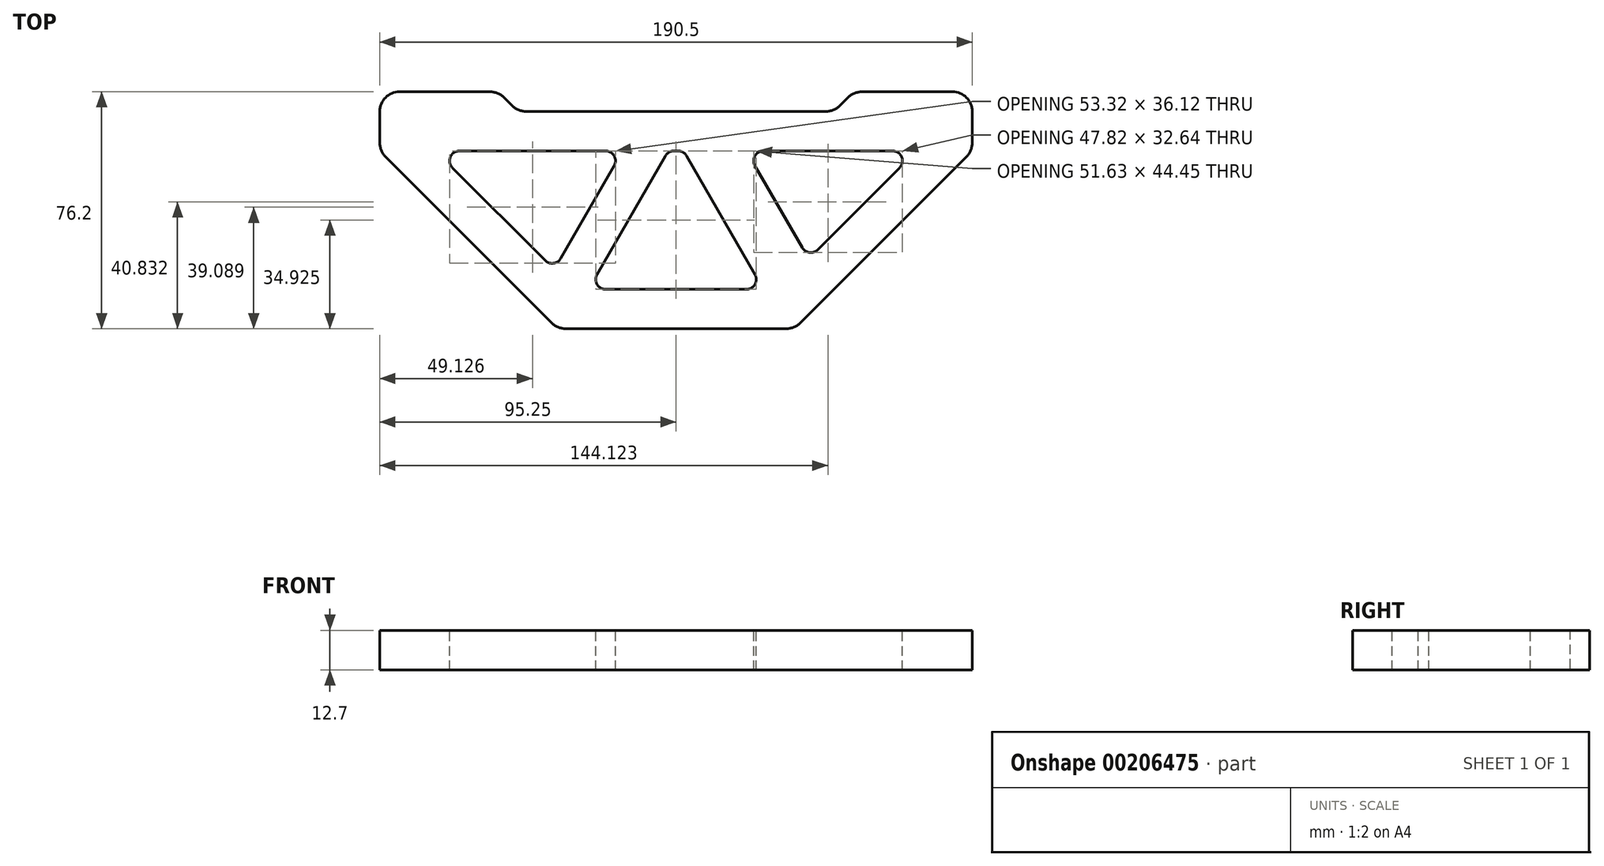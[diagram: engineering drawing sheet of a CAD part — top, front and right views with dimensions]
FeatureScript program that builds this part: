
annotation { "Feature Type Name" : "Feature", "Feature Type Description" : "" }
export const myFeature = defineFeature(function(context is Context, id is Id, definition is map)
    precondition{}
    {
        {
            var Q0;
            Q0=qCreatedBy(makeId("Top.planeOp"),FACE);
            var sketch = newSketch(context, id + "F0", { "sketchPlane" : qUnion([Q0])});
            skLineSegment(sketch, "E0", {"start": v(-82.55, 31.75) * mm, "end": v(-53.43, 31.75) * mm});
            skLineSegment(sketch, "E1", {"start": v(-48.94, 29.9) * mm, "end": v(-46.3, 27.26) * mm});
            skLineSegment(sketch, "E2", {"start": v(-41.82, 25.4) * mm, "end": v(54.52, 25.4) * mm});
            skLineSegment(sketch, "E3", {"start": v(59, 27.26) * mm, "end": v(61.64, 29.9) * mm});
            skLineSegment(sketch, "E4", {"start": v(66.13, 31.75) * mm, "end": v(95.25, 31.75) * mm});
            skLineSegment(sketch, "E5", {"start": v(101.6, 25.4) * mm, "end": v(101.6, 15.33) * mm});
            skLineSegment(sketch, "E6", {"start": v(99.74, 10.84) * mm, "end": v(46.3, -42.6) * mm});
            skLineSegment(sketch, "E7", {"start": v(41.82, -44.45) * mm, "end": v(-29.12, -44.45) * mm});
            skLineSegment(sketch, "E8", {"start": v(-33.6, -42.6) * mm, "end": v(-87.04, 10.84) * mm});
            skLineSegment(sketch, "E9", {"start": v(-88.9, 15.33) * mm, "end": v(-88.9, 25.4) * mm});
            skPoint(sketch, "E10.visualSharp", {"position": v(-88.9, 31.75) * mm});
            skArc(sketch, "E10.filletArc", {"start": v(-82.55, 31.75) * mm, "mid": v(-87.04, 29.9) * mm, "end": v(-88.9, 25.4) * mm});
            skPoint(sketch, "E11.visualSharp", {"position": v(-88.9, 12.7) * mm});
            skArc(sketch, "E11.filletArc", {"start": v(-88.9, 15.33) * mm, "mid": v(-88.42, 12.9) * mm, "end": v(-87.04, 10.84) * mm});
            skPoint(sketch, "E12.visualSharp", {"position": v(-31.75, -44.45) * mm});
            skArc(sketch, "E12.filletArc", {"start": v(-33.6, -42.6) * mm, "mid": v(-31.55, -43.97) * mm, "end": v(-29.12, -44.45) * mm});
            skPoint(sketch, "E13.visualSharp", {"position": v(44.45, -44.45) * mm});
            skArc(sketch, "E13.filletArc", {"start": v(41.82, -44.45) * mm, "mid": v(44.25, -43.97) * mm, "end": v(46.3, -42.6) * mm});
            skPoint(sketch, "E14.visualSharp", {"position": v(101.6, 12.7) * mm});
            skArc(sketch, "E14.filletArc", {"start": v(99.74, 10.84) * mm, "mid": v(101.12, 12.9) * mm, "end": v(101.6, 15.33) * mm});
            skPoint(sketch, "E15.visualSharp", {"position": v(101.6, 31.75) * mm});
            skArc(sketch, "E15.filletArc", {"start": v(101.6, 25.4) * mm, "mid": v(99.74, 29.9) * mm, "end": v(95.25, 31.75) * mm});
            skPoint(sketch, "E16.visualSharp", {"position": v(63.5, 31.75) * mm});
            skArc(sketch, "E16.filletArc", {"start": v(66.13, 31.75) * mm, "mid": v(63.7, 31.27) * mm, "end": v(61.64, 29.9) * mm});
            skPoint(sketch, "E17.visualSharp", {"position": v(57.15, 25.4) * mm});
            skArc(sketch, "E17.filletArc", {"start": v(54.52, 25.4) * mm, "mid": v(56.95, 25.88) * mm, "end": v(59, 27.26) * mm});
            skPoint(sketch, "E18.visualSharp", {"position": v(-44.45, 25.4) * mm});
            skArc(sketch, "E18.filletArc", {"start": v(-46.3, 27.26) * mm, "mid": v(-44.25, 25.88) * mm, "end": v(-41.82, 25.4) * mm});
            skPoint(sketch, "E19.visualSharp", {"position": v(-50.8, 31.75) * mm});
            skArc(sketch, "E19.filletArc", {"start": v(-48.94, 29.9) * mm, "mid": v(-51, 31.27) * mm, "end": v(-53.43, 31.75) * mm});
            skSolve(sketch);
        }
        {
            var Q0;
            Q0 = qSketchRegion(id + "F0", true);
            extrude(context, id + "F1", {"entities" : qUnion([Q0]), "depth" : 12.7 * mm});
        }
        {
            var Q0;
            Q0=makeQuery(id+"F1.opExtrude","CAP_FACE",FACE,{"disambiguationData":[OSD([sQuery(id+"F0.wireOp",EDGE,"E0"),sQuery(id+"F0.wireOp",EDGE,"E1"),sQuery(id+"F0.wireOp",EDGE,"E2"),sQuery(id+"F0.wireOp",EDGE,"E3"),sQuery(id+"F0.wireOp",EDGE,"E4"),sQuery(id+"F0.wireOp",EDGE,"E5"),sQuery(id+"F0.wireOp",EDGE,"E6"),sQuery(id+"F0.wireOp",EDGE,"E7"),sQuery(id+"F0.wireOp",EDGE,"E8"),sQuery(id+"F0.wireOp",EDGE,"E9"),sQuery(id+"F0.wireOp",EDGE,"E10.filletArc"),sQuery(id+"F0.wireOp",EDGE,"E11.filletArc"),sQuery(id+"F0.wireOp",EDGE,"E12.filletArc"),sQuery(id+"F0.wireOp",EDGE,"E13.filletArc"),sQuery(id+"F0.wireOp",EDGE,"E14.filletArc"),sQuery(id+"F0.wireOp",EDGE,"E15.filletArc"),sQuery(id+"F0.wireOp",EDGE,"E16.filletArc"),sQuery(id+"F0.wireOp",EDGE,"E17.filletArc"),sQuery(id+"F0.wireOp",EDGE,"E18.filletArc"),sQuery(id+"F0.wireOp",EDGE,"E19.filletArc")])],"isStart":false});
            var sketch = newSketch(context, id + "F2", { "sketchPlane" : qUnion([Q0])});
            skLineSegment(sketch, "E20", {"start": v(2.96, 11.11) * mm, "end": v(-19.04, -26.99) * mm});
            skLineSegment(sketch, "E21", {"start": v(-16.29, -31.75) * mm, "end": v(28.99, -31.75) * mm});
            skLineSegment(sketch, "E22", {"start": v(31.74, -26.99) * mm, "end": v(9.74, 11.11) * mm});
            skLineSegment(sketch, "E23", {"start": v(5.7, 12.7) * mm, "end": v(7, 12.7) * mm});
            skLineSegment(sketch, "E24", {"start": v(31.74, 7.94) * mm, "end": v(46.92, -18.36) * mm});
            skLineSegment(sketch, "E25", {"start": v(51.92, -19.02) * mm, "end": v(78.22, 7.28) * mm});
            skLineSegment(sketch, "E26", {"start": v(75.97, 12.7) * mm, "end": v(34.49, 12.7) * mm});
            skLineSegment(sketch, "E27", {"start": v(-65.52, 7.28) * mm, "end": v(-35.73, -22.5) * mm});
            skLineSegment(sketch, "E28", {"start": v(-30.74, -21.85) * mm, "end": v(-13.54, 7.94) * mm});
            skLineSegment(sketch, "E29", {"start": v(-16.29, 12.7) * mm, "end": v(-63.27, 12.7) * mm});
            skPoint(sketch, "E30.visualSharp", {"position": v(-70.94, 12.7) * mm});
            skArc(sketch, "E30.filletArc", {"start": v(-63.27, 12.7) * mm, "mid": v(-66.2, 10.74) * mm, "end": v(-65.52, 7.28) * mm});
            skPoint(sketch, "E31.visualSharp", {"position": v(-10.79, 12.7) * mm});
            skArc(sketch, "E31.filletArc", {"start": v(-13.54, 7.94) * mm, "mid": v(-13.54, 11.11) * mm, "end": v(-16.29, 12.7) * mm});
            skPoint(sketch, "E32.visualSharp", {"position": v(-21.79, -31.75) * mm});
            skArc(sketch, "E32.filletArc", {"start": v(-19.04, -26.99) * mm, "mid": v(-19.04, -30.16) * mm, "end": v(-16.29, -31.75) * mm});
            skPoint(sketch, "E33.visualSharp", {"position": v(34.49, -31.75) * mm});
            skArc(sketch, "E33.filletArc", {"start": v(28.99, -31.75) * mm, "mid": v(31.74, -30.16) * mm, "end": v(31.74, -26.99) * mm});
            skPoint(sketch, "E34.visualSharp", {"position": v(28.99, 12.7) * mm});
            skArc(sketch, "E34.filletArc", {"start": v(34.49, 12.7) * mm, "mid": v(31.74, 11.11) * mm, "end": v(31.74, 7.94) * mm});
            skPoint(sketch, "E35.visualSharp", {"position": v(49, -21.95) * mm});
            skArc(sketch, "E35.filletArc", {"start": v(46.92, -18.36) * mm, "mid": v(49.26, -19.92) * mm, "end": v(51.92, -19.02) * mm});
            skPoint(sketch, "E36.visualSharp", {"position": v(83.64, 12.7) * mm});
            skArc(sketch, "E36.filletArc", {"start": v(78.22, 7.28) * mm, "mid": v(78.9, 10.74) * mm, "end": v(75.97, 12.7) * mm});
            skPoint(sketch, "E37.visualSharp", {"position": v(8.82, 12.7) * mm});
            skArc(sketch, "E37.filletArc", {"start": v(9.74, 11.11) * mm, "mid": v(8.58, 12.27) * mm, "end": v(7, 12.7) * mm});
            skPoint(sketch, "E38.visualSharp", {"position": v(-32.8, -25.43) * mm});
            skArc(sketch, "E38.filletArc", {"start": v(-35.73, -22.5) * mm, "mid": v(-33.07, -23.41) * mm, "end": v(-30.74, -21.85) * mm});
            skPoint(sketch, "E39.visualSharp", {"position": v(3.88, 12.7) * mm});
            skArc(sketch, "E39.filletArc", {"start": v(5.7, 12.7) * mm, "mid": v(4.12, 12.27) * mm, "end": v(2.96, 11.11) * mm});
            skSolve(sketch);
        }
        {
            var Q0;
            Q0 = qSketchRegion(id + "F2", true);
            extrude(context, id + "F3", {"entities" : qUnion([Q0]), "operationType" : NewBodyOperationType.REMOVE, "endBound" : BoundingType.THROUGH_ALL, "oppositeDirection" : true, "depth" : 25.4 * mm});
        }
    });
